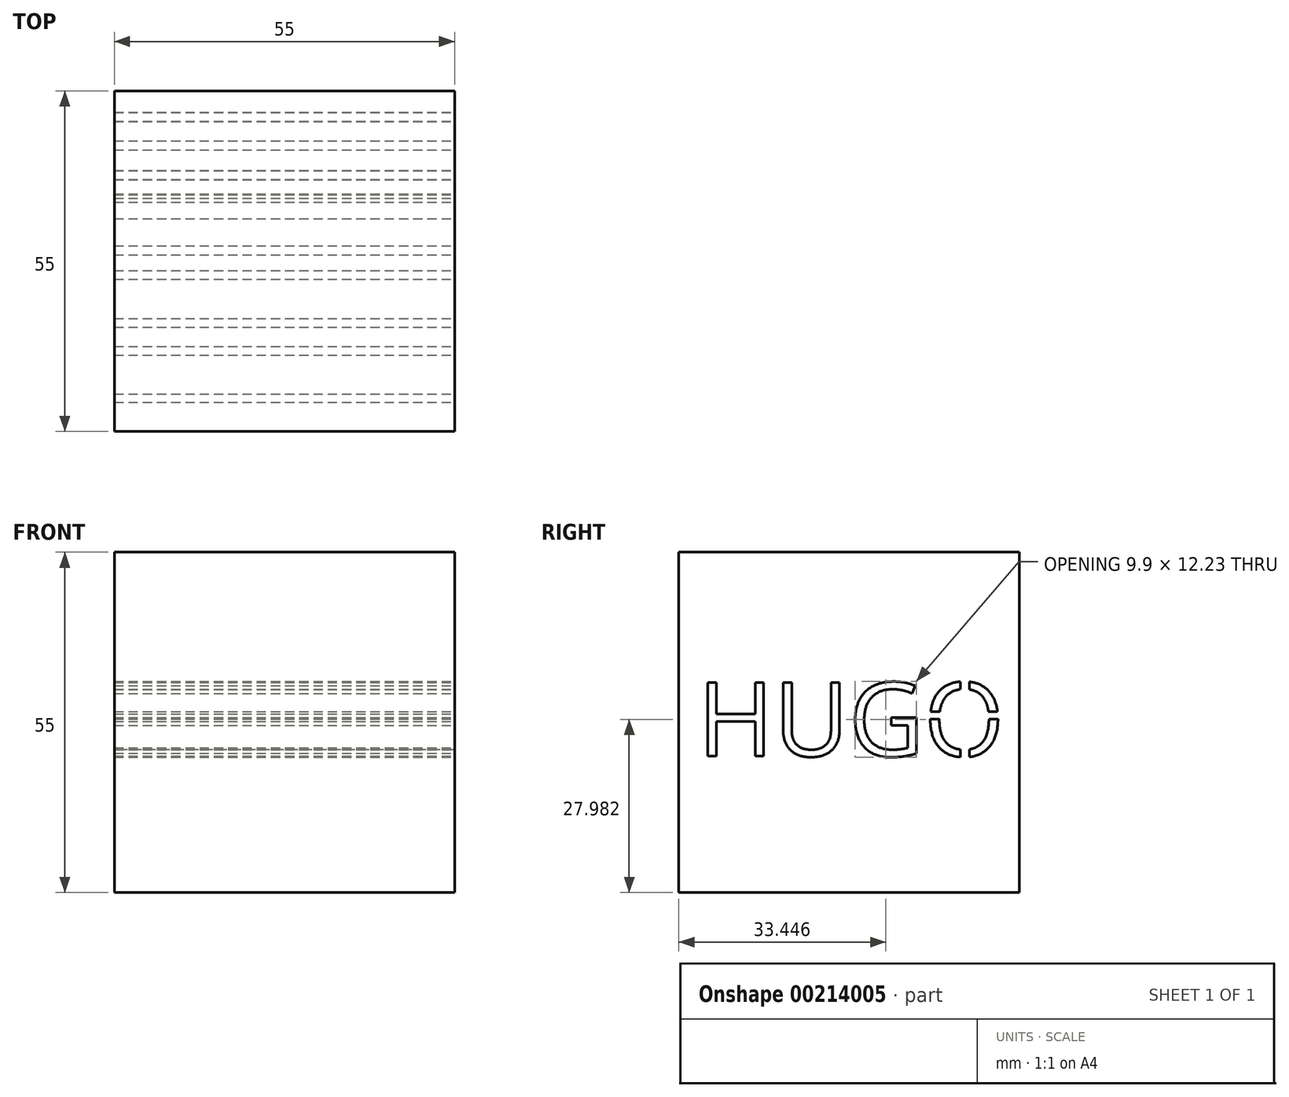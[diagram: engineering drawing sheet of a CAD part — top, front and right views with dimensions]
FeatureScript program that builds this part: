
annotation { "Feature Type Name" : "Feature", "Feature Type Description" : "" }
export const myFeature = defineFeature(function(context is Context, id is Id, definition is map)
    precondition{}
    {
        {
            var Q0;
            Q0=qCreatedBy(makeId("Right.planeOp"),FACE);
            var sketch = newSketch(context, id + "F0", { "sketchPlane" : qUnion([Q0])});
            skLineSegment(sketch, "E0", {"start": v(0, 0) * mm, "end": v(-55, 0) * mm});
            skLineSegment(sketch, "E1", {"start": v(-55, 0) * mm, "end": v(-55, 55) * mm});
            skLineSegment(sketch, "E2", {"start": v(0, 0) * mm, "end": v(0, 55) * mm});
            skLineSegment(sketch, "E3", {"start": v(-55, 55) * mm, "end": v(0, 55) * mm});
            skSolve(sketch);
        }
        {
            var Q0;
            Q0 = qSketchRegion(id + "F0", true);
            extrude(context, id + "F1", {"entities" : qUnion([Q0]), "depth" : 55 * mm});
        }
        {
            var Q0;
            Q0=makeQuery(id+"F1.opExtrude","CAP_FACE",FACE,{"disambiguationData":[OSD([sQuery(id+"F0.wireOp",EDGE,"E0"),sQuery(id+"F0.wireOp",EDGE,"E1"),sQuery(id+"F0.wireOp",EDGE,"E2"),sQuery(id+"F0.wireOp",EDGE,"E3")])],"isStart":false});
            var sketch = newSketch(context, id + "F2", { "sketchPlane" : qUnion([Q0])});
            skText(sketch, "E4", { "text": "HUGO ", "fontName": "OpenSans-Regular.ttf"});
            const initialGuessF2  = {"E4": [-0.05195, 0.02203, 1, 0, 0.012]};
            skSetInitialGuess(sketch, initialGuessF2);
            skSolve(sketch);
        }
        {
            var Q0;
            Q0 = qSketchRegion(id + "F2", true);
            extrude(context, id + "F3", {"entities" : qUnion([Q0]), "operationType" : NewBodyOperationType.REMOVE, "endBound" : BoundingType.THROUGH_ALL, "oppositeDirection" : true, "depth" : 25 * mm});
        }
        {
            var Q0;
            {var subQ0=sQuery(id+"F0.wireOp",EDGE,"E1");var subQ1=sQuery(id+"F0.wireOp",EDGE,"E3");var subQ2=sQuery(id+"F0.wireOp",EDGE,"E0");var subQ3=sQuery(id+"F0.wireOp",EDGE,"E2");Q0=makeQuery(id+"F3.boolean.opBoolean","SPLIT",FACE,{"disambiguationData":[TD([makeQuery(id+"F1.opExtrude","SWEPT_FACE",FACE,{"disambiguationData":[OSD([subQ2])]})])],"derivedFrom":makeQuery(id+"F1.opExtrude","CAP_FACE",FACE,{"disambiguationData":[OSD([subQ2,subQ0,subQ3,subQ1])],"isStart":true})});}
            var sketch = newSketch(context, id + "F4", { "sketchPlane" : qUnion([Q0])});
            skLineSegment(sketch, "E5.bottom", {"start": v(15.32, 28.01) * mm, "end": v(2.17, 28.01) * mm});
            skLineSegment(sketch, "E5.top", {"start": v(15.32, 29.21) * mm, "end": v(2.17, 29.21) * mm});
            skLineSegment(sketch, "E5.left", {"start": v(15.32, 28.01) * mm, "end": v(15.32, 29.21) * mm});
            skLineSegment(sketch, "E5.right", {"start": v(2.17, 28.01) * mm, "end": v(2.17, 29.21) * mm});
            skPoint(sketch, "E5.middle", {"position": v(8.74, 28.61) * mm});
            skLineSegment(sketch, "E6.bottom", {"start": v(9.5, 34.8) * mm, "end": v(8.05, 34.8) * mm});
            skLineSegment(sketch, "E6.top", {"start": v(9.5, 20.63) * mm, "end": v(8.05, 20.63) * mm});
            skLineSegment(sketch, "E6.left", {"start": v(9.5, 34.8) * mm, "end": v(9.5, 20.63) * mm});
            skLineSegment(sketch, "E6.right", {"start": v(8.05, 34.8) * mm, "end": v(8.05, 20.63) * mm});
            skSolve(sketch);
        }
        {
            var Q0;
            Q0 = qSketchRegion(id + "F4", true);
            var Q1;
            {var subQ0=sQuery(id+"F0.wireOp",EDGE,"E1");var subQ1=sQuery(id+"F0.wireOp",EDGE,"E3");var subQ2=sQuery(id+"F0.wireOp",EDGE,"E0");var subQ3=sQuery(id+"F0.wireOp",EDGE,"E2");Q1=makeQuery(id+"F3.boolean.opBoolean","SPLIT",FACE,{"disambiguationData":[TD([makeQuery(id+"F1.opExtrude","SWEPT_FACE",FACE,{"disambiguationData":[OSD([subQ2])]})])],"derivedFrom":makeQuery(id+"F1.opExtrude","CAP_FACE",FACE,{"disambiguationData":[OSD([subQ2,subQ0,subQ3,subQ1])],"isStart":false})});}
            extrude(context, id + "F5", {"entities" : qUnion([Q0]), "operationType" : NewBodyOperationType.ADD, "endBound" : BoundingType.UP_TO_SURFACE, "oppositeDirection" : true, "endBoundEntityFace" : qUnion([Q1]), "depth" : 25 * mm});
        }
    });
